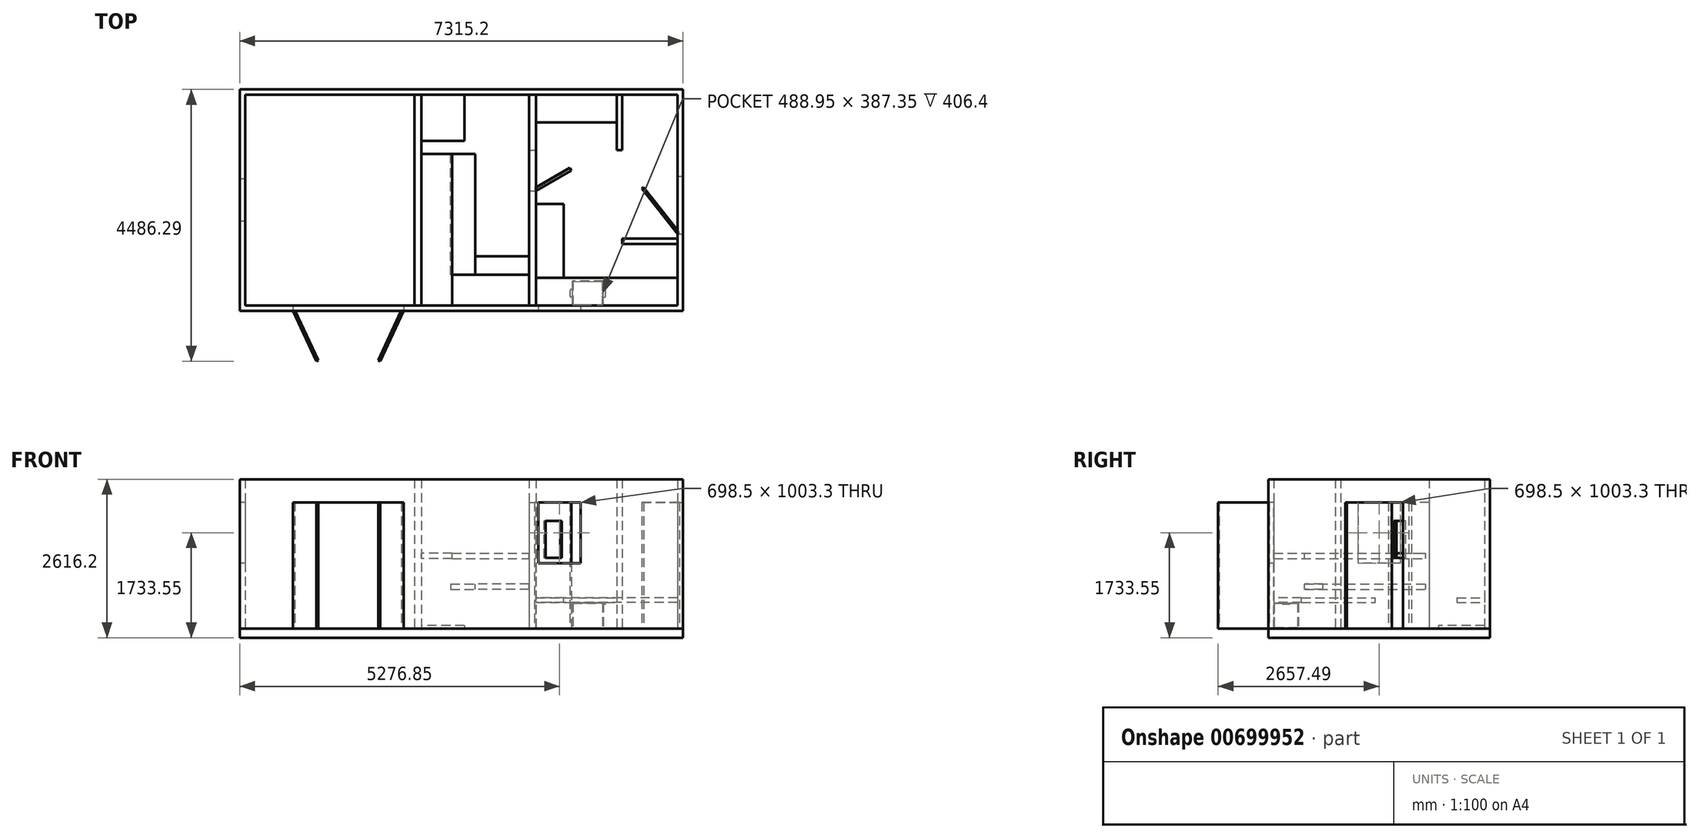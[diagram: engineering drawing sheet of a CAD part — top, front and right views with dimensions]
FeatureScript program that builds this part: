
annotation { "Feature Type Name" : "Feature", "Feature Type Description" : "" }
export const myFeature = defineFeature(function(context is Context, id is Id, definition is map)
    precondition{}
    {
        {
            var Q0;
            Q0=qCreatedBy(makeId("Top.planeOp"),FACE);
            var sketch = newSketch(context, id + "F0", { "sketchPlane" : qUnion([Q0])});
            skLineSegment(sketch, "E0.bottom", {"start": v(-3657.6, -1828.8) * mm, "end": v(3657.6, -1828.8) * mm});
            skLineSegment(sketch, "E0.top", {"start": v(-3657.6, 1828.8) * mm, "end": v(3657.6, 1828.8) * mm});
            skLineSegment(sketch, "E0.left", {"start": v(-3657.6, -1828.8) * mm, "end": v(-3657.6, 1828.8) * mm});
            skLineSegment(sketch, "E0.right", {"start": v(3657.6, -1828.8) * mm, "end": v(3657.6, 1828.8) * mm});
            skPoint(sketch, "E0.middle", {"position": v(0, 0) * mm});
            skSolve(sketch);
        }
        {
            var Q0;
            Q0=makeQuery(id+"F0.imprint","IMPRINT",FACE,{"disambiguationData":[TD([[makeQuery(id+"F0.imprint","IMPRINT",EDGE,{"derivedFrom":sQuery(id+"F0.wireOp",EDGE,"E0.bottom")}),1.0]])]});
            extrude(context, id + "F1", {"entities" : qUnion([Q0]), "depth" : 152.4 * mm});
        }
        {
            var Q0;
            Q0=makeQuery(id+"F1.opExtrude","CAP_FACE",FACE,{"disambiguationData":[OSD([sQuery(id+"F0.wireOp",EDGE,"E0.bottom"),sQuery(id+"F0.wireOp",EDGE,"E0.top"),sQuery(id+"F0.wireOp",EDGE,"E0.left"),sQuery(id+"F0.wireOp",EDGE,"E0.right")])],"isStart":false});
            var sketch = newSketch(context, id + "F2", { "sketchPlane" : qUnion([Q0])});
            skLineSegment(sketch, "E1.0", {"start": v(-3657.6, -1828.8) * mm, "end": v(-3657.6, 1828.8) * mm});
            skLineSegment(sketch, "E1.1", {"start": v(-3657.6, 1828.8) * mm, "end": v(3657.6, 1828.8) * mm});
            skLineSegment(sketch, "E1.2", {"start": v(3657.6, -1828.8) * mm, "end": v(3657.6, 1828.8) * mm});
            skLineSegment(sketch, "E1.3", {"start": v(-3657.6, -1828.8) * mm, "end": v(3657.6, -1828.8) * mm});
            skLineSegment(sketch, "E2.bottom", {"start": v(-3568.7, 1739.9) * mm, "end": v(3568.7, 1739.9) * mm});
            skLineSegment(sketch, "E2.top", {"start": v(-3568.7, -1739.9) * mm, "end": v(3568.7, -1739.9) * mm});
            skLineSegment(sketch, "E2.left", {"start": v(-3568.7, 1739.9) * mm, "end": v(-3568.7, -1739.9) * mm});
            skLineSegment(sketch, "E2.right", {"start": v(3568.7, 1739.9) * mm, "end": v(3568.7, -1739.9) * mm});
            skLineSegment(sketch, "E3", {"start": v(3568.7, 0) * mm, "end": v(0, 0) * mm, "construction": true});
            skSolve(sketch);
        }
        {
            var Q0;
            Q0=qSketchRegion(id+"F2",true);
            extrude(context, id + "F3", {"entities" : qUnion([Q0]), "depth" : 2463.8 * mm});
        }
        {
            var Q0;
            Q0=makeQuery(id+"F3.opExtrude","SWEPT_FACE",FACE,{"disambiguationData":[OSD([sQuery(id+"F2.wireOp",EDGE,"E1.2")])]});
            var sketch = newSketch(context, id + "F4", { "sketchPlane" : qUnion([Q0])});
            skLineSegment(sketch, "E4.bottom", {"start": v(-558.8, 152.4) * mm, "end": v(393.7, 152.4) * mm});
            skLineSegment(sketch, "E4.top", {"start": v(-558.8, 2235.2) * mm, "end": v(393.7, 2235.2) * mm});
            skLineSegment(sketch, "E4.left", {"start": v(-558.8, 152.4) * mm, "end": v(-558.8, 2235.2) * mm});
            skLineSegment(sketch, "E4.right", {"start": v(393.7, 152.4) * mm, "end": v(393.7, 2235.2) * mm});
            skSolve(sketch);
        }
        {
            var Q0;
            Q0=qSketchRegion(id+"F4",true);
            extrude(context, id + "F5", {"entities" : qUnion([Q0]), "operationType" : NewBodyOperationType.REMOVE, "endBound" : BoundingType.UP_TO_NEXT, "oppositeDirection" : true, "depth" : 25.4 * mm});
        }
        {
            var Q0;
            Q0=makeQuery(id+"F3.opExtrude","SWEPT_FACE",FACE,{"disambiguationData":[OSD([sQuery(id+"F2.wireOp",EDGE,"E1.3")])]});
            var sketch = newSketch(context, id + "F6", { "sketchPlane" : qUnion([Q0])});
            skLineSegment(sketch, "E5.bottom", {"start": v(-2781.3, 152.4) * mm, "end": v(-952.5, 152.4) * mm});
            skLineSegment(sketch, "E5.top", {"start": v(-2781.3, 2235.2) * mm, "end": v(-952.5, 2235.2) * mm});
            skLineSegment(sketch, "E5.left", {"start": v(-2781.3, 152.4) * mm, "end": v(-2781.3, 2235.2) * mm});
            skLineSegment(sketch, "E5.right", {"start": v(-952.5, 152.4) * mm, "end": v(-952.5, 2235.2) * mm});
            skLineSegment(sketch, "E6.bottom", {"start": v(1270, 2235.2) * mm, "end": v(1968.5, 2235.2) * mm});
            skLineSegment(sketch, "E6.top", {"start": v(1270, 1231.9) * mm, "end": v(1968.5, 1231.9) * mm});
            skLineSegment(sketch, "E6.left", {"start": v(1270, 2235.2) * mm, "end": v(1270, 1231.9) * mm});
            skLineSegment(sketch, "E6.right", {"start": v(1968.5, 2235.2) * mm, "end": v(1968.5, 1231.9) * mm});
            skSolve(sketch);
        }
        {
            var Q0;
            Q0=qSketchRegion(id+"F6",true);
            extrude(context, id + "F7", {"entities" : qUnion([Q0]), "operationType" : NewBodyOperationType.REMOVE, "endBound" : BoundingType.UP_TO_NEXT, "oppositeDirection" : true, "depth" : 25.4 * mm});
        }
        {
            var Q0;
            Q0=makeQuery(id+"F3.opExtrude","SWEPT_FACE",FACE,{"disambiguationData":[OSD([sQuery(id+"F2.wireOp",EDGE,"E1.0")])]});
            var sketch = newSketch(context, id + "F8", { "sketchPlane" : qUnion([Q0])});
            skLineSegment(sketch, "E7.bottom", {"start": v(-349.25, 2235.2) * mm, "end": v(349.25, 2235.2) * mm});
            skLineSegment(sketch, "E7.top", {"start": v(-349.25, 1231.9) * mm, "end": v(349.25, 1231.9) * mm});
            skLineSegment(sketch, "E7.left", {"start": v(-349.25, 2235.2) * mm, "end": v(-349.25, 1231.9) * mm});
            skLineSegment(sketch, "E7.right", {"start": v(349.25, 2235.2) * mm, "end": v(349.25, 1231.9) * mm});
            skLineSegment(sketch, "E8", {"start": v(0, 2235.2) * mm, "end": v(0, 1231.9) * mm, "construction": true});
            skSolve(sketch);
        }
        {
            var Q0;
            Q0=qSketchRegion(id+"F8",true);
            extrude(context, id + "F9", {"entities" : qUnion([Q0]), "operationType" : NewBodyOperationType.REMOVE, "endBound" : BoundingType.UP_TO_NEXT, "oppositeDirection" : true, "depth" : 25.4 * mm});
        }
        {
            var Q0;
            Q0=makeQuery(id+"F1.opExtrude","CAP_FACE",FACE,{"disambiguationData":[OSD([sQuery(id+"F0.wireOp",EDGE,"E0.bottom"),sQuery(id+"F0.wireOp",EDGE,"E0.top"),sQuery(id+"F0.wireOp",EDGE,"E0.left"),sQuery(id+"F0.wireOp",EDGE,"E0.right")])],"isStart":false});
            var sketch = newSketch(context, id + "F10", { "sketchPlane" : qUnion([Q0])});
            skLineSegment(sketch, "E9.top", {"start": v(-774.7, 1739.9) * mm, "end": v(-660.4, 1739.9) * mm});
            skLineSegment(sketch, "E10.top", {"start": v(1117.6, 1739.9) * mm, "end": v(1231.9, 1739.9) * mm});
            skLineSegment(sketch, "E11", {"start": v(1117.6, 1739.9) * mm, "end": v(1117.6, -1739.9) * mm});
            skLineSegment(sketch, "E12", {"start": v(1231.9, -1739.9) * mm, "end": v(1231.9, 1739.9) * mm});
            skLineSegment(sketch, "E13", {"start": v(-660.4, -1739.9) * mm, "end": v(-660.4, 1739.9) * mm});
            skLineSegment(sketch, "E14", {"start": v(-774.7, -1739.9) * mm, "end": v(-774.7, 1739.9) * mm});
            skLineSegment(sketch, "E15", {"start": v(-774.7, -1739.9) * mm, "end": v(-660.4, -1739.9) * mm});
            skLineSegment(sketch, "E16", {"start": v(1117.6, -1739.9) * mm, "end": v(1231.9, -1739.9) * mm});
            skSolve(sketch);
        }
        {
            var Q0;
            Q0=qSketchRegion(id+"F10",true);
            var Q1;
            Q1=makeQuery(id+"F3.opExtrude","CAP_FACE",FACE,{"disambiguationData":[OSD([sQuery(id+"F2.wireOp",EDGE,"E1.0"),sQuery(id+"F2.wireOp",EDGE,"E1.1"),sQuery(id+"F2.wireOp",EDGE,"E1.2"),sQuery(id+"F2.wireOp",EDGE,"E1.3"),sQuery(id+"F2.wireOp",EDGE,"E2.bottom"),sQuery(id+"F2.wireOp",EDGE,"E2.top"),sQuery(id+"F2.wireOp",EDGE,"E2.left"),sQuery(id+"F2.wireOp",EDGE,"E2.right")])],"isStart":false});
            extrude(context, id + "F11", {"entities" : qUnion([Q0]), "endBound" : BoundingType.UP_TO_SURFACE, "endBoundEntityFace" : qUnion([Q1]), "depth" : 25.4 * mm});
        }
        {
            var Q0;
            Q0=makeQuery(id+"F1.opExtrude","CAP_FACE",FACE,{"disambiguationData":[OSD([sQuery(id+"F0.wireOp",EDGE,"E0.bottom"),sQuery(id+"F0.wireOp",EDGE,"E0.top"),sQuery(id+"F0.wireOp",EDGE,"E0.left"),sQuery(id+"F0.wireOp",EDGE,"E0.right")])],"isStart":false});
            var sketch = newSketch(context, id + "F12", { "sketchPlane" : qUnion([Q0])});
            skLineSegment(sketch, "E17.bottom", {"start": v(3568.7, -723.9) * mm, "end": v(2654.3, -723.9) * mm});
            skLineSegment(sketch, "E17.top", {"start": v(3568.7, -635) * mm, "end": v(2654.3, -635) * mm});
            skLineSegment(sketch, "E17.left", {"start": v(3568.7, -723.9) * mm, "end": v(3568.7, -635) * mm});
            skLineSegment(sketch, "E17.right", {"start": v(2654.3, -723.9) * mm, "end": v(2654.3, -635) * mm});
            skSolve(sketch);
        }
        {
            var Q0;
            Q0=qSketchRegion(id+"F12",true);
            var Q1;
            Q1=makeQuery(id+"F3.opExtrude","CAP_FACE",FACE,{"disambiguationData":[OSD([sQuery(id+"F2.wireOp",EDGE,"E1.0"),sQuery(id+"F2.wireOp",EDGE,"E1.1"),sQuery(id+"F2.wireOp",EDGE,"E1.2"),sQuery(id+"F2.wireOp",EDGE,"E1.3"),sQuery(id+"F2.wireOp",EDGE,"E2.bottom"),sQuery(id+"F2.wireOp",EDGE,"E2.top"),sQuery(id+"F2.wireOp",EDGE,"E2.left"),sQuery(id+"F2.wireOp",EDGE,"E2.right")])],"isStart":false});
            extrude(context, id + "F13", {"entities" : qUnion([Q0]), "endBound" : BoundingType.UP_TO_SURFACE, "endBoundEntityFace" : qUnion([Q1]), "depth" : 25.4 * mm});
        }
        {
            var Q0;
            Q0=makeQuery(id+"F11.opExtrude","SWEPT_FACE",FACE,{"disambiguationData":[OSD([sQuery(id+"F10.wireOp",EDGE,"E12")])]});
            var sketch = newSketch(context, id + "F14", { "sketchPlane" : qUnion([Q0])});
            skLineSegment(sketch, "E18.bottom", {"start": v(152.4, 152.4) * mm, "end": v(825.5, 152.4) * mm});
            skLineSegment(sketch, "E18.top", {"start": v(152.4, 2235.2) * mm, "end": v(825.5, 2235.2) * mm});
            skLineSegment(sketch, "E18.left", {"start": v(152.4, 152.4) * mm, "end": v(152.4, 2235.2) * mm});
            skLineSegment(sketch, "E18.right", {"start": v(825.5, 152.4) * mm, "end": v(825.5, 2235.2) * mm});
            skSolve(sketch);
        }
        {
            var Q0;
            Q0=qSketchRegion(id+"F14",true);
            extrude(context, id + "F15", {"entities" : qUnion([Q0]), "operationType" : NewBodyOperationType.REMOVE, "endBound" : BoundingType.UP_TO_NEXT, "oppositeDirection" : true, "depth" : 25.4 * mm});
        }
        {
            var Q0;
            Q0=qCreatedBy(makeId("Front.planeOp"),FACE);
            var sketch = newSketch(context, id + "F16", { "sketchPlane" : qUnion([Q0])});
            skLineSegment(sketch, "E19.bottom", {"start": v(-660.4, 1397) * mm, "end": v(-152.4, 1397) * mm});
            skLineSegment(sketch, "E19.top", {"start": v(-660.4, 1308.1) * mm, "end": v(-152.4, 1308.1) * mm});
            skLineSegment(sketch, "E19.left", {"start": v(-660.4, 1397) * mm, "end": v(-660.4, 1308.1) * mm});
            skLineSegment(sketch, "E19.right", {"start": v(-152.4, 1397) * mm, "end": v(-152.4, 1308.1) * mm});
            skSolve(sketch);
        }
        {
            var Q0;
            Q0=qSketchRegion(id+"F16",true);
            extrude(context, id + "F17", {"entities" : qUnion([Q0]), "endBound" : BoundingType.UP_TO_NEXT, "depth" : 812.8 * mm, "hasSecondDirection" : true, "secondDirectionOppositeDirection" : true, "secondDirectionDepth" : 762 * mm, "offsetDistance" : 25.4 * mm});
        }
        {
            var Q0;
            Q0=makeQuery(id+"F17.opExtrude","SWEPT_FACE",FACE,{"disambiguationData":[OSD([sQuery(id+"F16.wireOp",EDGE,"E19.bottom")])]});
            var sketch = newSketch(context, id + "F18", { "sketchPlane" : qUnion([Q0])});
            skLineSegment(sketch, "E20.top", {"start": v(-152.4, -1739.9) * mm, "end": v(1117.6, -1739.9) * mm});
            skLineSegment(sketch, "E20.left", {"start": v(-152.4, -1739.9) * mm, "end": v(-152.4, -1231.9) * mm});
            skLineSegment(sketch, "E20.right", {"start": v(1117.6, -1739.9) * mm, "end": v(1117.6, -1231.9) * mm});
            skLineSegment(sketch, "E21", {"start": v(1117.6, -1231.9) * mm, "end": v(-152.4, -1231.9) * mm});
            skSolve(sketch);
        }
        {
            var Q0;
            Q0=qSketchRegion(id+"F18",true);
            var Q1;
            Q1=makeQuery(id+"F17.opExtrude","CAP_VERTEX",VERTEX,{"disambiguationData":[OSD([sQuery(id+"F2.wireOp",EDGE,"E2.top"),sQuery(id+"F16.wireOp",EDGE,"E19.top"),sQuery(id+"F16.wireOp",EDGE,"E19.right")])],"isStart":false});
            extrude(context, id + "F19", {"entities" : qUnion([Q0]), "endBound" : BoundingType.UP_TO_VERTEX, "oppositeDirection" : true, "endBoundEntityVertex" : qUnion([Q1]), "depth" : 25.4 * mm});
        }
        {
            var Q0;
            Q0=qCreatedBy(makeId("Front.planeOp"),FACE);
            var sketch = newSketch(context, id + "F20", { "sketchPlane" : qUnion([Q0])});
            skLineSegment(sketch, "E22.bottom", {"start": v(-177.8, 889) * mm, "end": v(228.6, 889) * mm});
            skLineSegment(sketch, "E22.top", {"start": v(-177.8, 800.1) * mm, "end": v(228.6, 800.1) * mm});
            skLineSegment(sketch, "E22.left", {"start": v(-177.8, 889) * mm, "end": v(-177.8, 800.1) * mm});
            skLineSegment(sketch, "E22.right", {"start": v(228.6, 889) * mm, "end": v(228.6, 800.1) * mm});
            skSolve(sketch);
        }
        {
            var Q0;
            Q0=qSketchRegion(id+"F20",true);
            extrude(context, id + "F21", {"entities" : qUnion([Q0]), "depth" : 1231.9 * mm, "hasSecondDirection" : true, "secondDirectionOppositeDirection" : true, "secondDirectionDepth" : 762 * mm, "offsetDistance" : 25.4 * mm});
        }
        {
            var Q0;
            Q0=makeQuery(id+"F21.opExtrude","SWEPT_FACE",FACE,{"disambiguationData":[OSD([sQuery(id+"F20.wireOp",EDGE,"E22.bottom")])]});
            var sketch = newSketch(context, id + "F22", { "sketchPlane" : qUnion([Q0])});
            skLineSegment(sketch, "E23.bottom", {"start": v(1117.6, -927.1) * mm, "end": v(228.6, -927.1) * mm});
            skLineSegment(sketch, "E23.top", {"start": v(228.6, -1231.9) * mm, "end": v(1117.6, -1231.9) * mm});
            skLineSegment(sketch, "E23.left", {"start": v(228.6, -927.1) * mm, "end": v(228.6, -1231.9) * mm});
            skLineSegment(sketch, "E23.right", {"start": v(1117.6, -927.1) * mm, "end": v(1117.6, -1231.9) * mm});
            skSolve(sketch);
        }
        {
            var Q0;
            Q0=makeQuery(id+"F3.opExtrude","SWEPT_FACE",FACE,{"disambiguationData":[OSD([sQuery(id+"F2.wireOp",EDGE,"E2.bottom")])]});
            var sketch = newSketch(context, id + "F23", { "sketchPlane" : qUnion([Q0])});
            skLineSegment(sketch, "E24.bottom", {"start": v(3568.7, 660.4) * mm, "end": v(2146.3, 660.4) * mm});
            skLineSegment(sketch, "E24.top", {"start": v(2146.3, 571.5) * mm, "end": v(3568.7, 571.5) * mm});
            skLineSegment(sketch, "E24.left", {"start": v(3568.7, 660.4) * mm, "end": v(3568.7, 571.5) * mm});
            skLineSegment(sketch, "E24.right", {"start": v(2146.3, 660.4) * mm, "end": v(2146.3, 571.5) * mm});
            skSolve(sketch);
        }
        {
            var Q0;
            Q0=qSketchRegion(id+"F22",true);
            var Q1;
            Q1=makeQuery(id+"F21.opExtrude","CAP_VERTEX",VERTEX,{"disambiguationData":[OSD([sQuery(id+"F20.wireOp",EDGE,"E22.top"),sQuery(id+"F20.wireOp",EDGE,"E22.right")])],"isStart":true});
            extrude(context, id + "F24", {"entities" : qUnion([Q0]), "endBound" : BoundingType.UP_TO_VERTEX, "oppositeDirection" : true, "endBoundEntityVertex" : qUnion([Q1]), "depth" : 25.4 * mm});
        }
        {
            var Q0;
            Q0=makeQuery(id+"F1.opExtrude","CAP_FACE",FACE,{"disambiguationData":[OSD([sQuery(id+"F0.wireOp",EDGE,"E0.bottom"),sQuery(id+"F0.wireOp",EDGE,"E0.top"),sQuery(id+"F0.wireOp",EDGE,"E0.left"),sQuery(id+"F0.wireOp",EDGE,"E0.right")])],"isStart":false});
            var sketch = newSketch(context, id + "F25", { "sketchPlane" : qUnion([Q0])});
            skLineSegment(sketch, "E25", {"start": v(1206.5, 196.4) * mm, "end": v(1231.9, 152.4) * mm});
            skLineSegment(sketch, "E26", {"start": v(1231.9, 152.4) * mm, "end": v(1814.82, 488.95) * mm});
            skLineSegment(sketch, "E27", {"start": v(1814.82, 488.95) * mm, "end": v(1789.42, 532.94) * mm});
            skLineSegment(sketch, "E28", {"start": v(1789.42, 532.94) * mm, "end": v(1206.5, 196.4) * mm});
            skSolve(sketch);
        }
        {
            var Q0;
            Q0=qSketchRegion(id+"F25",true);
            extrude(context, id + "F26", {"entities" : qUnion([Q0]), "depth" : 2082.8 * mm});
        }
        {
            var Q0;
            Q0=makeQuery(id+"F1.opExtrude","CAP_FACE",FACE,{"disambiguationData":[OSD([sQuery(id+"F0.wireOp",EDGE,"E0.bottom"),sQuery(id+"F0.wireOp",EDGE,"E0.top"),sQuery(id+"F0.wireOp",EDGE,"E0.left"),sQuery(id+"F0.wireOp",EDGE,"E0.right")])],"isStart":false});
            var sketch = newSketch(context, id + "F27", { "sketchPlane" : qUnion([Q0])});
            skLineSegment(sketch, "E29", {"start": v(3568.7, -558.8) * mm, "end": v(3598.59, -535.17) * mm});
            skLineSegment(sketch, "E30", {"start": v(3598.59, -535.17) * mm, "end": v(3007.81, 211.99) * mm});
            skLineSegment(sketch, "E31", {"start": v(3007.81, 211.99) * mm, "end": v(2977.93, 188.36) * mm});
            skLineSegment(sketch, "E32", {"start": v(2977.93, 188.36) * mm, "end": v(3568.7, -558.8) * mm});
            skSolve(sketch);
        }
        {
            var Q0;
            Q0=qSketchRegion(id+"F27",true);
            extrude(context, id + "F28", {"entities" : qUnion([Q0]), "depth" : 2082.8 * mm});
        }
        {
            var Q0;
            Q0=makeQuery(id+"F3.opExtrude","SWEPT_FACE",FACE,{"disambiguationData":[OSD([sQuery(id+"F2.wireOp",EDGE,"E2.top")])]});
            var sketch = newSketch(context, id + "F29", { "sketchPlane" : qUnion([Q0])});
            skLineSegment(sketch, "E33.bottom", {"start": v(-3568.7, 660.4) * mm, "end": v(-1231.9, 660.4) * mm});
            skLineSegment(sketch, "E33.top", {"start": v(-3568.7, 584.2) * mm, "end": v(-1231.9, 584.2) * mm});
            skLineSegment(sketch, "E33.left", {"start": v(-3568.7, 660.4) * mm, "end": v(-3568.7, 584.2) * mm});
            skLineSegment(sketch, "E33.right", {"start": v(-1231.9, 660.4) * mm, "end": v(-1231.9, 584.2) * mm});
            skSolve(sketch);
        }
        {
            var Q0;
            Q0=qSketchRegion(id+"F29",true);
            extrude(context, id + "F30", {"entities" : qUnion([Q0]), "depth" : 457.2 * mm, "offsetDistance" : 25.4 * mm});
        }
        {
            var Q0;
            Q0=makeQuery(id+"F26.opExtrude","SWEPT_FACE",FACE,{"disambiguationData":[OSD([sQuery(id+"F25.wireOp",EDGE,"E26")])]});
            var sketch = newSketch(context, id + "F31", { "sketchPlane" : qUnion([Q0])});
            skLineSegment(sketch, "E34.bottom", {"start": v(1327.2, 1930.4) * mm, "end": v(1632, 1930.4) * mm});
            skLineSegment(sketch, "E34.top", {"start": v(1327.2, 1320.8) * mm, "end": v(1632, 1320.8) * mm});
            skLineSegment(sketch, "E34.left", {"start": v(1327.2, 1930.4) * mm, "end": v(1327.2, 1320.8) * mm});
            skLineSegment(sketch, "E34.right", {"start": v(1632, 1930.4) * mm, "end": v(1632, 1320.8) * mm});
            skLineSegment(sketch, "E35", {"start": v(1479.6, 2235.2) * mm, "end": v(1479.6, 1930.4) * mm, "construction": true});
            skSolve(sketch);
        }
        {
            var Q0;
            Q0=qSketchRegion(id+"F31",true);
            extrude(context, id + "F32", {"entities" : qUnion([Q0]), "operationType" : NewBodyOperationType.REMOVE, "endBound" : BoundingType.UP_TO_NEXT, "oppositeDirection" : true, "depth" : 25.4 * mm});
        }
        {
            var Q0;
            Q0=makeQuery(id+"F1.opExtrude","CAP_FACE",FACE,{"disambiguationData":[OSD([sQuery(id+"F0.wireOp",EDGE,"E0.bottom"),sQuery(id+"F0.wireOp",EDGE,"E0.top"),sQuery(id+"F0.wireOp",EDGE,"E0.left"),sQuery(id+"F0.wireOp",EDGE,"E0.right")])],"isStart":false});
            var sketch = newSketch(context, id + "F33", { "sketchPlane" : qUnion([Q0])});
            skLineSegment(sketch, "E36", {"start": v(50.8, 977.9) * mm, "end": v(-660.4, 977.9) * mm});
            skLineSegment(sketch, "E37", {"start": v(-660.4, 977.9) * mm, "end": v(-660.4, 1739.9) * mm});
            skLineSegment(sketch, "E38", {"start": v(-660.4, 1739.9) * mm, "end": v(50.8, 1739.9) * mm});
            skLineSegment(sketch, "E39", {"start": v(50.8, 1739.9) * mm, "end": v(50.8, 1358.9) * mm});
            skLineSegment(sketch, "E40.trimOffspring", {"start": v(50.8, 1358.9) * mm, "end": v(50.8, 977.9) * mm});
            skSolve(sketch);
        }
        {
            var Q0;
            Q0=qSketchRegion(id+"F33",true);
            extrude(context, id + "F34", {"entities" : qUnion([Q0]), "depth" : 50.8 * mm});
        }
        {
            var Q0;
            Q0=makeQuery(id+"F1.opExtrude","CAP_FACE",FACE,{"disambiguationData":[OSD([sQuery(id+"F0.wireOp",EDGE,"E0.bottom"),sQuery(id+"F0.wireOp",EDGE,"E0.top"),sQuery(id+"F0.wireOp",EDGE,"E0.left"),sQuery(id+"F0.wireOp",EDGE,"E0.right")])],"isStart":false});
            var sketch = newSketch(context, id + "F35", { "sketchPlane" : qUnion([Q0])});
            skLineSegment(sketch, "E41.bottom", {"start": v(2343, -1739.9) * mm, "end": v(1835, -1739.9) * mm});
            skLineSegment(sketch, "E41.top", {"start": v(2343, -1333.5) * mm, "end": v(1835, -1333.5) * mm});
            skLineSegment(sketch, "E41.left", {"start": v(2343, -1739.9) * mm, "end": v(2343, -1333.5) * mm});
            skLineSegment(sketch, "E41.right", {"start": v(1835, -1739.9) * mm, "end": v(1835, -1333.5) * mm});
            skSolve(sketch);
        }
        {
            var Q0;
            Q0=qSketchRegion(id+"F35",true);
            extrude(context, id + "F36", {"entities" : qUnion([Q0]), "depth" : 9.52 * mm});
        }
        {
            var Q0;
            Q0=makeQuery(id+"F36.opExtrude","CAP_FACE",FACE,{"disambiguationData":[OSD([sQuery(id+"F35.wireOp",EDGE,"E41.bottom"),sQuery(id+"F35.wireOp",EDGE,"E41.top"),sQuery(id+"F35.wireOp",EDGE,"E41.left"),sQuery(id+"F35.wireOp",EDGE,"E41.right")])],"isStart":false});
            var sketch = newSketch(context, id + "F37", { "sketchPlane" : qUnion([Q0])});
            skLineSegment(sketch, "E42", {"start": v(2343, -1739.9) * mm, "end": v(2343, -1333.5) * mm});
            skLineSegment(sketch, "E43", {"start": v(2343, -1333.5) * mm, "end": v(1835, -1333.5) * mm});
            skLineSegment(sketch, "E44", {"start": v(1835, -1333.5) * mm, "end": v(1835, -1739.9) * mm});
            skLineSegment(sketch, "E45", {"start": v(1835, -1739.9) * mm, "end": v(2343, -1739.9) * mm});
            skLineSegment(sketch, "E46.0", {"start": v(1844.52, -1730.38) * mm, "end": v(2333.47, -1730.38) * mm});
            skLineSegment(sketch, "E46.1", {"start": v(1844.52, -1343.02) * mm, "end": v(1844.52, -1730.38) * mm});
            skLineSegment(sketch, "E46.2", {"start": v(2333.47, -1343.02) * mm, "end": v(1844.52, -1343.02) * mm});
            skLineSegment(sketch, "E46.3", {"start": v(2333.47, -1730.38) * mm, "end": v(2333.47, -1343.02) * mm});
            skSolve(sketch);
        }
        {
            var Q0;
            Q0=qSketchRegion(id+"F37",true);
            extrude(context, id + "F38", {"entities" : qUnion([Q0]), "operationType" : NewBodyOperationType.ADD, "depth" : 406.4 * mm});
        }
        {
            var Q0;
            Q0=makeQuery(id+"F38.opExtrude","CAP_FACE",FACE,{"disambiguationData":[OSD([sQuery(id+"F37.wireOp",EDGE,"E42"),sQuery(id+"F37.wireOp",EDGE,"E43"),sQuery(id+"F37.wireOp",EDGE,"E44"),sQuery(id+"F37.wireOp",EDGE,"E45"),sQuery(id+"F37.wireOp",EDGE,"E46.0"),sQuery(id+"F37.wireOp",EDGE,"E46.1"),sQuery(id+"F37.wireOp",EDGE,"E46.2"),sQuery(id+"F37.wireOp",EDGE,"E46.3")])],"isStart":false});
            var sketch = newSketch(context, id + "F39", { "sketchPlane" : qUnion([Q0])});
            skLineSegment(sketch, "E47.bottom", {"start": v(1835, -1600.2) * mm, "end": v(1809.6, -1600.2) * mm});
            skLineSegment(sketch, "E47.top", {"start": v(1835, -1473.2) * mm, "end": v(1809.6, -1473.2) * mm});
            skLineSegment(sketch, "E47.left", {"start": v(1835, -1600.2) * mm, "end": v(1835, -1473.2) * mm});
            skLineSegment(sketch, "E47.right", {"start": v(1796.9, -1587.5) * mm, "end": v(1796.9, -1485.9) * mm});
            skLineSegment(sketch, "E48.bottom", {"start": v(2343, -1600.2) * mm, "end": v(2368.4, -1600.2) * mm});
            skLineSegment(sketch, "E48.top", {"start": v(2343, -1473.2) * mm, "end": v(2368.4, -1473.2) * mm});
            skLineSegment(sketch, "E48.left", {"start": v(2343, -1600.2) * mm, "end": v(2343, -1473.2) * mm});
            skLineSegment(sketch, "E48.right", {"start": v(2381.1, -1587.5) * mm, "end": v(2381.1, -1485.9) * mm});
            skPoint(sketch, "E49.visualSharp", {"position": v(2381.1, -1600.2) * mm});
            skArc(sketch, "E49.filletArc", {"start": v(2368.4, -1600.2) * mm, "mid": v(2377.38, -1596.48) * mm, "end": v(2381.1, -1587.5) * mm});
            skPoint(sketch, "E50.visualSharp", {"position": v(2381.1, -1473.2) * mm});
            skArc(sketch, "E50.filletArc", {"start": v(2381.1, -1485.9) * mm, "mid": v(2377.38, -1476.92) * mm, "end": v(2368.4, -1473.2) * mm});
            skPoint(sketch, "E51.visualSharp", {"position": v(1796.9, -1600.2) * mm});
            skArc(sketch, "E51.filletArc", {"start": v(1796.9, -1587.5) * mm, "mid": v(1800.62, -1596.48) * mm, "end": v(1809.6, -1600.2) * mm});
            skPoint(sketch, "E52.visualSharp", {"position": v(1796.9, -1473.2) * mm});
            skArc(sketch, "E52.filletArc", {"start": v(1809.6, -1473.2) * mm, "mid": v(1800.62, -1476.92) * mm, "end": v(1796.9, -1485.9) * mm});
            skPoint(sketch, "E53", {"position": v(2333.47, -1536.7) * mm});
            skLineSegment(sketch, "E54", {"start": v(2343, -1536.7) * mm, "end": v(1835, -1536.7) * mm, "construction": true});
            skSolve(sketch);
        }
        {
            var Q0;
            Q0=qSketchRegion(id+"F39",true);
            extrude(context, id + "F40", {"entities" : qUnion([Q0]), "operationType" : NewBodyOperationType.ADD, "oppositeDirection" : true, "depth" : 12.7 * mm});
        }
        {
            var Q0;
            Q0=makeQuery(id+"F1.opExtrude","CAP_FACE",FACE,{"disambiguationData":[OSD([sQuery(id+"F0.wireOp",EDGE,"E0.bottom"),sQuery(id+"F0.wireOp",EDGE,"E0.top"),sQuery(id+"F0.wireOp",EDGE,"E0.left"),sQuery(id+"F0.wireOp",EDGE,"E0.right")])],"isStart":false});
            var sketch = newSketch(context, id + "F41", { "sketchPlane" : qUnion([Q0])});
            skLineSegment(sketch, "E55", {"start": v(-2781.3, -1828.8) * mm, "end": v(-2746.77, -1812.7) * mm});
            skLineSegment(sketch, "E56", {"start": v(-2746.77, -1812.7) * mm, "end": v(-2360.25, -2641.39) * mm});
            skLineSegment(sketch, "E57", {"start": v(-2360.25, -2641.39) * mm, "end": v(-2394.78, -2657.5) * mm});
            skLineSegment(sketch, "E58", {"start": v(-2394.78, -2657.5) * mm, "end": v(-2781.3, -1828.8) * mm});
            skLineSegment(sketch, "E59", {"start": v(-952.5, -1828.8) * mm, "end": v(-987.03, -1812.7) * mm});
            skLineSegment(sketch, "E60", {"start": v(-987.03, -1812.7) * mm, "end": v(-1373.55, -2641.39) * mm});
            skLineSegment(sketch, "E61", {"start": v(-1373.55, -2641.39) * mm, "end": v(-1339.02, -2657.5) * mm});
            skLineSegment(sketch, "E62", {"start": v(-1339.02, -2657.5) * mm, "end": v(-952.5, -1828.8) * mm});
            skSolve(sketch);
        }
        {
            var Q0;
            Q0=qSketchRegion(id+"F41",true);
            extrude(context, id + "F42", {"entities" : qUnion([Q0]), "depth" : 2082.8 * mm, "offsetDistance" : 25.4 * mm});
        }
        {
            var Q0;
            Q0=makeQuery(id+"F1.opExtrude","CAP_FACE",FACE,{"disambiguationData":[OSD([sQuery(id+"F0.wireOp",EDGE,"E0.bottom"),sQuery(id+"F0.wireOp",EDGE,"E0.top"),sQuery(id+"F0.wireOp",EDGE,"E0.left"),sQuery(id+"F0.wireOp",EDGE,"E0.right")])],"isStart":false});
            var sketch = newSketch(context, id + "F43", { "sketchPlane" : qUnion([Q0])});
            skLineSegment(sketch, "E63.bottom", {"start": v(2565.4, 1739.9) * mm, "end": v(2654.3, 1739.9) * mm});
            skLineSegment(sketch, "E63.top", {"start": v(2565.4, 825.5) * mm, "end": v(2654.3, 825.5) * mm});
            skLineSegment(sketch, "E63.left", {"start": v(2565.4, 1739.9) * mm, "end": v(2565.4, 825.5) * mm});
            skLineSegment(sketch, "E63.right", {"start": v(2654.3, 1739.9) * mm, "end": v(2654.3, 825.5) * mm});
            skSolve(sketch);
        }
        {
            var Q0;
            Q0=qSketchRegion(id+"F43",true);
            extrude(context, id + "F44", {"entities" : qUnion([Q0]), "depth" : 2463.8 * mm, "offsetDistance" : 25.4 * mm});
        }
        {
            var Q0;
            Q0=makeQuery(id+"F30.opExtrude","SWEPT_FACE",FACE,{"disambiguationData":[OSD([sQuery(id+"F29.wireOp",EDGE,"E33.bottom")])]});
            var sketch = newSketch(context, id + "F45", { "sketchPlane" : qUnion([Q0])});
            skLineSegment(sketch, "E64.bottom", {"start": v(1231.9, -1282.7) * mm, "end": v(1689.1, -1282.7) * mm});
            skLineSegment(sketch, "E64.top", {"start": v(1231.9, -63.5) * mm, "end": v(1689.1, -63.5) * mm});
            skLineSegment(sketch, "E64.left", {"start": v(1231.9, -1282.7) * mm, "end": v(1231.9, -63.5) * mm});
            skLineSegment(sketch, "E64.right", {"start": v(1689.1, -1282.7) * mm, "end": v(1689.1, -63.5) * mm});
            skSolve(sketch);
        }
        {
            var Q0;
            Q0=qSketchRegion(id+"F45",true);
            extrude(context, id + "F46", {"entities" : qUnion([Q0]), "oppositeDirection" : true, "depth" : 76.2 * mm, "offsetDistance" : 25.4 * mm});
        }
        {
            var Q0;
            Q0=makeQuery(id+"F3.opExtrude","SWEPT_FACE",FACE,{"disambiguationData":[OSD([sQuery(id+"F2.wireOp",EDGE,"E2.bottom")])]});
            var sketch = newSketch(context, id + "F47", { "sketchPlane" : qUnion([Q0])});
            skLineSegment(sketch, "E65.bottom", {"start": v(1231.9, 660.4) * mm, "end": v(2565.4, 660.4) * mm});
            skLineSegment(sketch, "E65.top", {"start": v(1231.9, 584.2) * mm, "end": v(2565.4, 584.2) * mm});
            skLineSegment(sketch, "E65.left", {"start": v(1231.9, 660.4) * mm, "end": v(1231.9, 584.2) * mm});
            skLineSegment(sketch, "E65.right", {"start": v(2565.4, 660.4) * mm, "end": v(2565.4, 584.2) * mm});
            skSolve(sketch);
        }
        {
            var Q0;
            Q0 = qSketchRegion(id + "F47", true);
            extrude(context, id + "F48", {"entities" : qUnion([Q0]), "depth" : 457.2 * mm, "offsetDistance" : 25.4 * mm});
        }
    });
